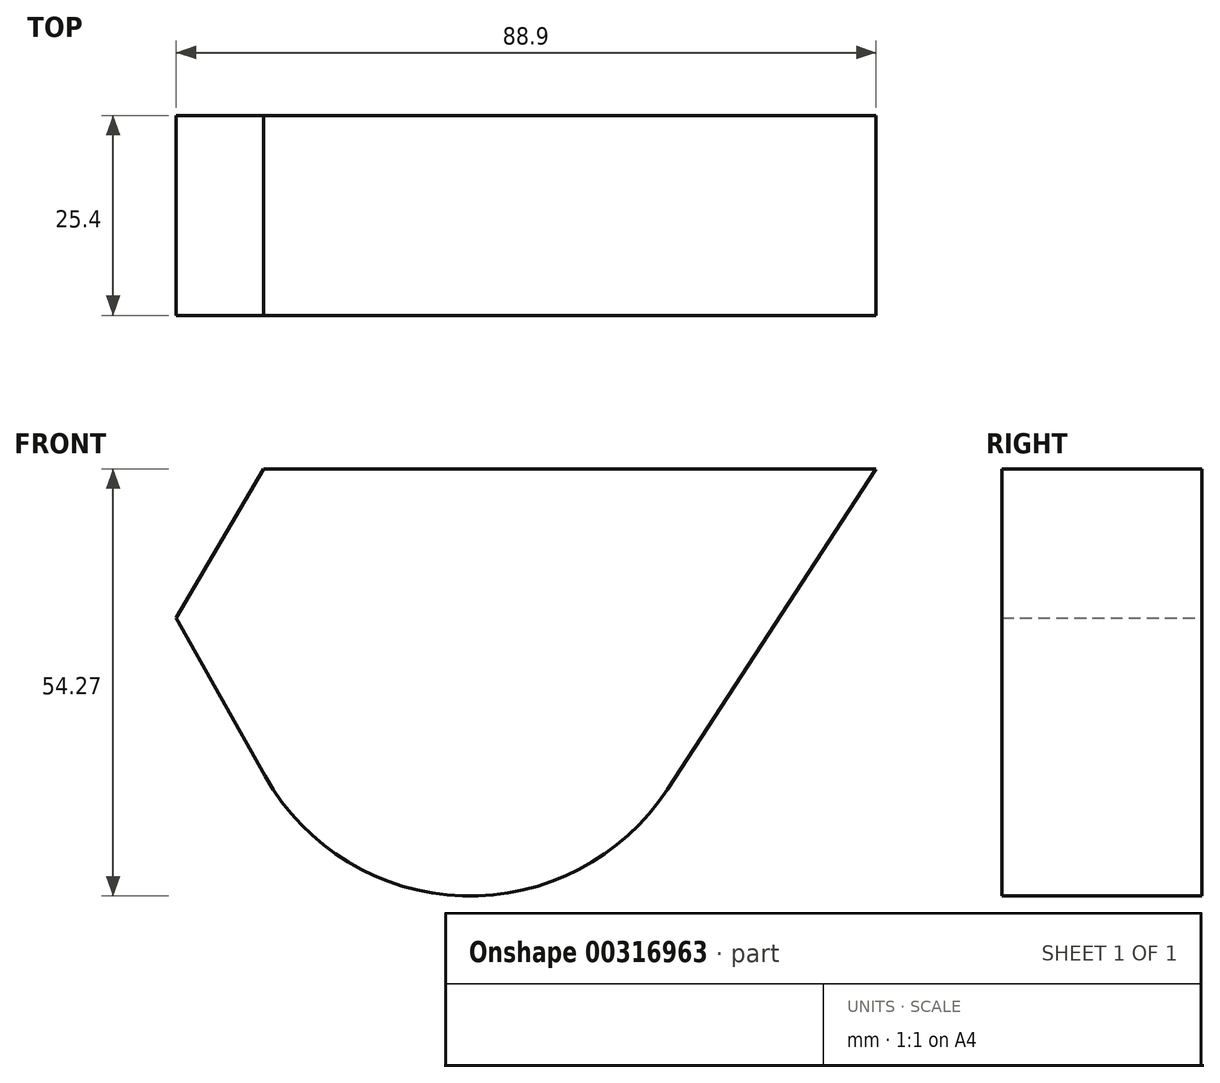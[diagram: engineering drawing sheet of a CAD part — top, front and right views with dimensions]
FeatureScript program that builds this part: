
annotation { "Feature Type Name" : "Feature", "Feature Type Description" : "" }
export const myFeature = defineFeature(function(context is Context, id is Id, definition is map)
    precondition{}
    {
        {
            var Q0;
            Q0=qCreatedBy(makeId("Front.planeOp"),FACE);
            var sketch = newSketch(context, id + "F0", { "sketchPlane" : qUnion([Q0])});
            skLineSegment(sketch, "E0", {"start": v(-46.1, 36.9) * mm, "end": v(53.43, 36.9) * mm});
            skLineSegment(sketch, "E1", {"start": v(53.43, 36.9) * mm, "end": v(0, -45.15) * mm});
            skLineSegment(sketch, "E2", {"start": v(0, -45.15) * mm, "end": v(-46.1, 36.9) * mm});
            skSolve(sketch);
        }
        {
            var Q0;
            Q0 = qSketchRegion(id + "F0", true);
            extrude(context, id + "F1", {"entities" : qUnion([Q0]), "depth" : 25.4 * mm});
        }
        {
            var Q0;
            Q0=makeQuery(id+"F1.opExtrude","SWEPT_EDGE",EDGE,{"disambiguationData":[OSD([sQuery(id+"F0.wireOp",EDGE,"E0"),sQuery(id+"F0.wireOp",EDGE,"E2")])]});
            chamfer(context, id + "F2", {"entities" : qUnion([Q0]), "width" : 12.7 * mm, "tangentPropagation" : true});
        }
        {
            var Q0;
            Q0=makeQuery(id+"F1.opExtrude","SWEPT_EDGE",EDGE,{"disambiguationData":[OSD([sQuery(id+"F0.wireOp",EDGE,"E1"),sQuery(id+"F0.wireOp",EDGE,"E2")])]});
            fillet(context, id + "F3", {"entities" : qUnion([Q0]), "radius" : 29.9 * mm, "tangentPropagation" : true, "allowEdgeOverflow" : false});
        }
    });
